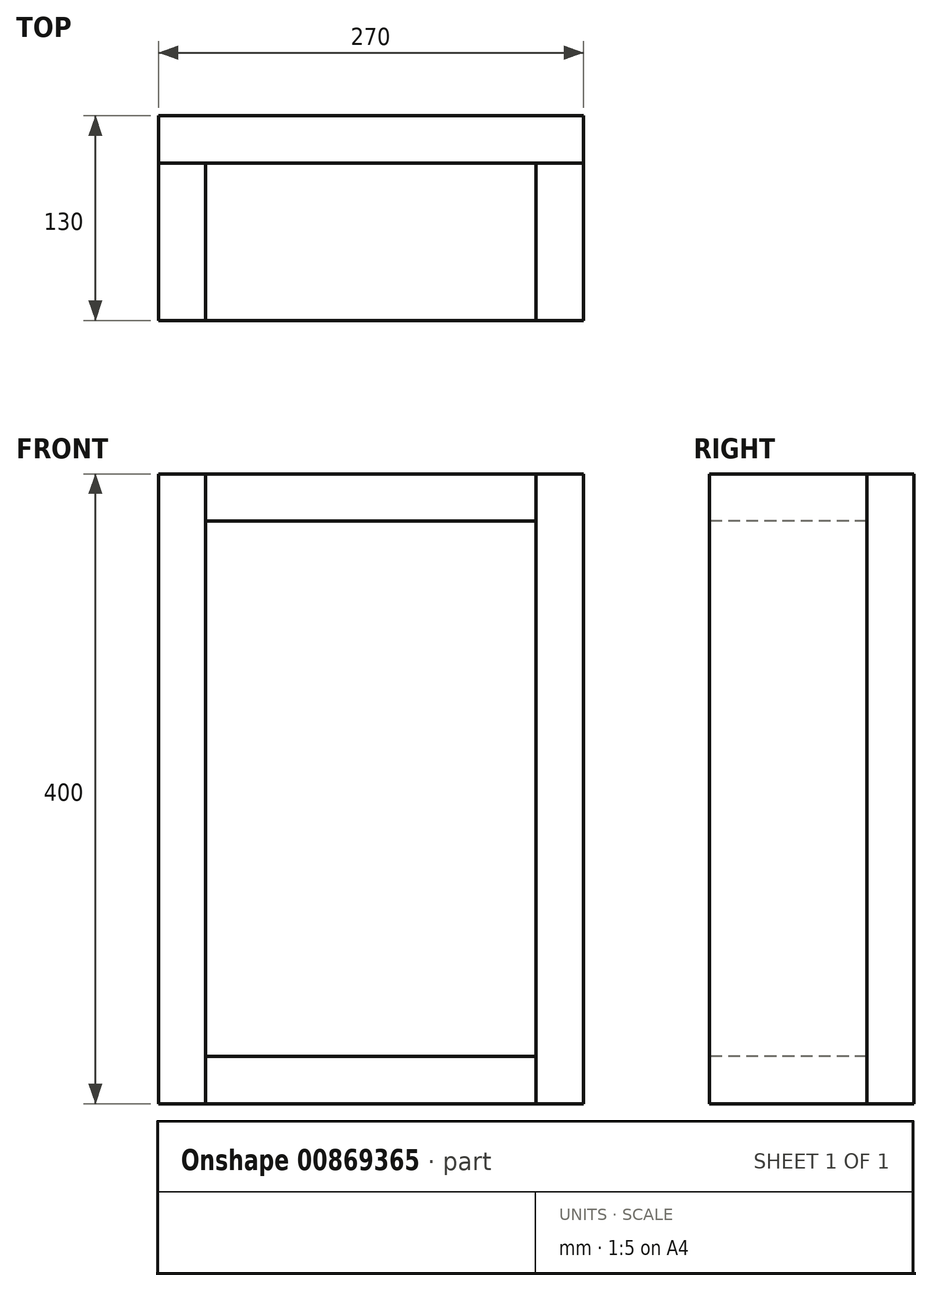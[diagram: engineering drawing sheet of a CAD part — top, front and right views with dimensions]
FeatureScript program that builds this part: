
annotation { "Feature Type Name" : "Feature", "Feature Type Description" : "" }
export const myFeature = defineFeature(function(context is Context, id is Id, definition is map)
    precondition{}
    {
        {
            var Q0;
            Q0=qCreatedBy(makeId("Right.planeOp"),FACE);
            var sketch = newSketch(context, id + "F0", { "sketchPlane" : qUnion([Q0])});
            skLineSegment(sketch, "E0.bottom", {"start": v(0, 0) * mm, "end": v(-30, 0) * mm});
            skLineSegment(sketch, "E0.top", {"start": v(0, -400) * mm, "end": v(-30, -400) * mm});
            skLineSegment(sketch, "E0.left", {"start": v(0, 0) * mm, "end": v(0, -400) * mm});
            skLineSegment(sketch, "E0.right", {"start": v(-30, 0) * mm, "end": v(-30, -400) * mm});
            skLineSegment(sketch, "E1.bottom", {"start": v(-30, 0) * mm, "end": v(-130, 0) * mm});
            skLineSegment(sketch, "E1.top", {"start": v(-30, -30) * mm, "end": v(-130, -30) * mm});
            skLineSegment(sketch, "E1.left", {"start": v(-30, 0) * mm, "end": v(-30, -30) * mm});
            skLineSegment(sketch, "E1.right", {"start": v(-130, 0) * mm, "end": v(-130, -30) * mm});
            skLineSegment(sketch, "E2.bottom", {"start": v(-30, -400) * mm, "end": v(-130, -400) * mm});
            skLineSegment(sketch, "E2.top", {"start": v(-30, -370) * mm, "end": v(-130, -370) * mm});
            skLineSegment(sketch, "E2.left", {"start": v(-30, -400) * mm, "end": v(-30, -370) * mm});
            skLineSegment(sketch, "E2.right", {"start": v(-130, -400) * mm, "end": v(-130, -370) * mm});
            skSolve(sketch);
        }
        {
            var Q0;
            {var subQ4=sQuery(id+"F0.wireOp",EDGE,"E0.bottom");Q0=makeQuery(id+"F0.imprint","IMPRINT",FACE,{"disambiguationData":[TD([[makeQuery(id+"F0.imprint","IMPRINT",EDGE,{"derivedFrom":subQ4}),1.0]])]});}
            extrude(context, id + "F1", {"entities" : qUnion([Q0]), "endBound" : BoundingType.SYMMETRIC, "depth" : 270 * mm, "offsetDistance" : 25 * mm});
        }
        {
            var Q0;
            {var subQ0=sQuery(id+"F0.wireOp",EDGE,"E1.bottom");Q0=makeQuery(id+"F0.imprint","IMPRINT",FACE,{"disambiguationData":[TD([[makeQuery(id+"F0.imprint","IMPRINT",EDGE,{"derivedFrom":subQ0}),1.0]])]});}
            extrude(context, id + "F2", {"entities" : qUnion([Q0]), "endBound" : BoundingType.SYMMETRIC, "depth" : 210 * mm, "offsetDistance" : 25 * mm});
        }
        {
            var Q0;
            {var subQ0=sQuery(id+"F0.wireOp",EDGE,"E2.bottom");Q0=makeQuery(id+"F0.imprint","IMPRINT",FACE,{"disambiguationData":[TD([[makeQuery(id+"F0.imprint","IMPRINT",EDGE,{"derivedFrom":subQ0}),-1.0]])]});}
            extrude(context, id + "F3", {"entities" : qUnion([Q0]), "endBound" : BoundingType.SYMMETRIC, "depth" : 210 * mm, "offsetDistance" : 25 * mm});
        }
        {
            var Q0;
            Q0=makeQuery(id+"F1.opExtrude","SWEPT_FACE",FACE,{"disambiguationData":[OSD([sQuery(id+"F0.wireOp",EDGE,"E0.right")])]});
            var sketch = newSketch(context, id + "F4", { "sketchPlane" : qUnion([Q0])});
            skPoint(sketch, "E3.0", {"position": v(-105, 0) * mm});
            skPoint(sketch, "E3.1", {"position": v(105, 0) * mm});
            skLineSegment(sketch, "E4.bottom", {"start": v(-105, 0) * mm, "end": v(-135, 0) * mm});
            skLineSegment(sketch, "E4.top", {"start": v(-105, -400) * mm, "end": v(-135, -400) * mm});
            skLineSegment(sketch, "E4.left", {"start": v(-105, 0) * mm, "end": v(-105, -400) * mm});
            skLineSegment(sketch, "E4.right", {"start": v(-135, 0) * mm, "end": v(-135, -400) * mm});
            skLineSegment(sketch, "E5.bottom", {"start": v(105, 0) * mm, "end": v(135, 0) * mm});
            skLineSegment(sketch, "E5.top", {"start": v(105, -400) * mm, "end": v(135, -400) * mm});
            skLineSegment(sketch, "E5.left", {"start": v(105, 0) * mm, "end": v(105, -400) * mm});
            skLineSegment(sketch, "E5.right", {"start": v(135, 0) * mm, "end": v(135, -400) * mm});
            skSolve(sketch);
        }
        {
            var Q0;
            Q0=makeQuery(id+"F4.imprint","IMPRINT",FACE,{"disambiguationData":[TD([[makeQuery(id+"F4.imprint","IMPRINT",EDGE,{"derivedFrom":sQuery(id+"F4.wireOp",EDGE,"E4.bottom")}),1.0]])]});
            var Q1;
            Q1=makeQuery(id+"F2.opExtrude","SWEPT_FACE",FACE,{"disambiguationData":[OSD([sQuery(id+"F0.wireOp",EDGE,"E1.right")])]});
            extrude(context, id + "F5", {"entities" : qUnion([Q0]), "endBound" : BoundingType.UP_TO_SURFACE, "depth" : 25 * mm, "endBoundEntityFace" : qUnion([Q1]), "offsetDistance" : 25 * mm});
        }
        {
            var Q0;
            Q0=makeQuery(id+"F4.imprint","IMPRINT",FACE,{"disambiguationData":[TD([[makeQuery(id+"F4.imprint","IMPRINT",EDGE,{"derivedFrom":sQuery(id+"F4.wireOp",EDGE,"E5.bottom")}),1.0]])]});
            var Q1;
            Q1=makeQuery(id+"F2.opExtrude","SWEPT_FACE",FACE,{"disambiguationData":[OSD([sQuery(id+"F0.wireOp",EDGE,"E1.right")])]});
            extrude(context, id + "F6", {"entities" : qUnion([Q0]), "endBound" : BoundingType.UP_TO_SURFACE, "depth" : 25 * mm, "endBoundEntityFace" : qUnion([Q1]), "offsetDistance" : 25 * mm});
        }
    });
